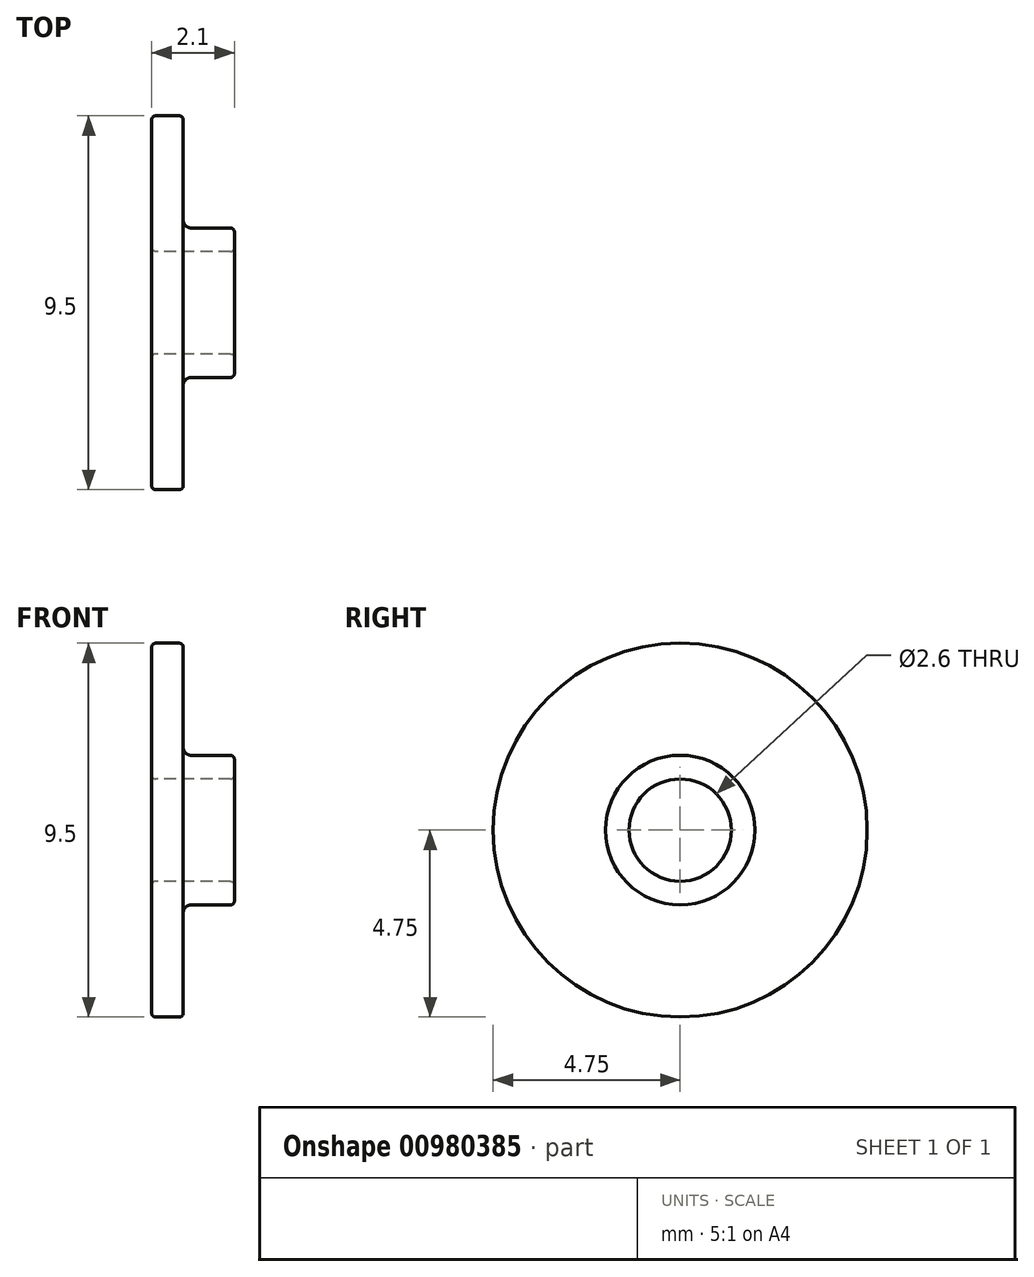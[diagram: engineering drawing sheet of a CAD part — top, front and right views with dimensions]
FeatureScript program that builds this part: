
annotation { "Feature Type Name" : "Feature", "Feature Type Description" : "" }
export const myFeature = defineFeature(function(context is Context, id is Id, definition is map)
    precondition{}
    {
        {
            var Q0;
            Q0=qCreatedBy(makeId("Front.planeOp"),FACE);
            var sketch = newSketch(context, id + "F0", { "sketchPlane" : qUnion([Q0])});
            skLineSegment(sketch, "E0", {"start": v(0.1, 4.75) * mm, "end": v(0.7, 4.75) * mm});
            skLineSegment(sketch, "E1", {"start": v(0.8, 4.65) * mm, "end": v(0.8, 2.1) * mm});
            skLineSegment(sketch, "E2", {"start": v(1, 1.9) * mm, "end": v(2, 1.9) * mm});
            skLineSegment(sketch, "E3", {"start": v(2.1, 1.8) * mm, "end": v(2.1, 1.4) * mm});
            skLineSegment(sketch, "E4", {"start": v(2, 1.3) * mm, "end": v(0.1, 1.3) * mm});
            skLineSegment(sketch, "E5", {"start": v(0, 1.4) * mm, "end": v(0, 4.65) * mm});
            skPoint(sketch, "E6.visualSharp", {"position": v(0.8, 1.9) * mm});
            skArc(sketch, "E6.filletArc", {"start": v(0.8, 2.1) * mm, "mid": v(0.86, 1.96) * mm, "end": v(1, 1.9) * mm});
            skPoint(sketch, "E7.visualSharp", {"position": v(0, 4.75) * mm});
            skArc(sketch, "E7.filletArc", {"start": v(0.1, 4.75) * mm, "mid": v(0.03, 4.72) * mm, "end": v(0, 4.65) * mm});
            skPoint(sketch, "E8.visualSharp", {"position": v(0.8, 4.75) * mm});
            skArc(sketch, "E8.filletArc", {"start": v(0.8, 4.65) * mm, "mid": v(0.77, 4.72) * mm, "end": v(0.7, 4.75) * mm});
            skPoint(sketch, "E9.visualSharp", {"position": v(0, 1.3) * mm});
            skArc(sketch, "E9.filletArc", {"start": v(0, 1.4) * mm, "mid": v(0.03, 1.33) * mm, "end": v(0.1, 1.3) * mm});
            skPoint(sketch, "E10.visualSharp", {"position": v(2.1, 1.3) * mm});
            skArc(sketch, "E10.filletArc", {"start": v(2, 1.3) * mm, "mid": v(2.07, 1.33) * mm, "end": v(2.1, 1.4) * mm});
            skPoint(sketch, "E11.visualSharp", {"position": v(2.1, 1.9) * mm});
            skArc(sketch, "E11.filletArc", {"start": v(2.1, 1.8) * mm, "mid": v(2.07, 1.87) * mm, "end": v(2, 1.9) * mm});
            skLineSegment(sketch, "E12", {"start": v(-1.82, 0) * mm, "end": v(4.74, 0) * mm, "construction": true});
            skSolve(sketch);
        }
        {
            var Q0;
            Q0=makeQuery(id+"F0.imprint","IMPRINT",FACE,{"disambiguationData":[TD([[makeQuery(id+"F0.imprint","IMPRINT",EDGE,{"derivedFrom":sQuery(id+"F0.wireOp",EDGE,"E0")}),-1.0]])]});
            var Q1;
            Q1=sQuery(id+"F0.wireOp",EDGE,"E12");
            revolve(context, id + "F1", {"surfaceOperationType" : NewSurfaceOperationType.NEW, "entities" : qUnion([Q0]), "axis" : qUnion([Q1]), "revolveType" : RevolveType.FULL});
        }
    });
